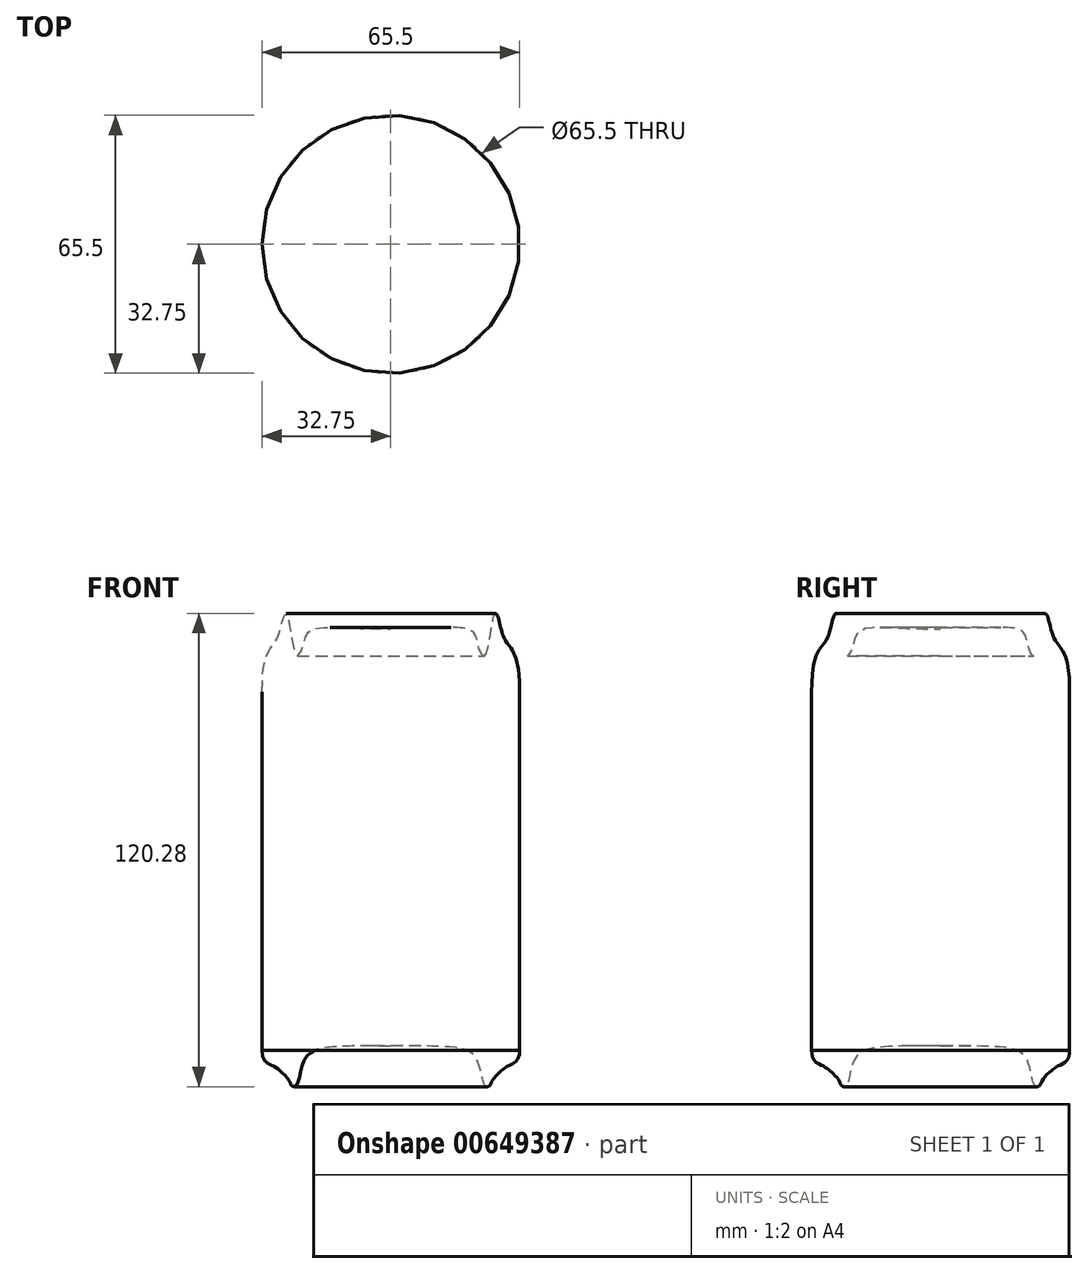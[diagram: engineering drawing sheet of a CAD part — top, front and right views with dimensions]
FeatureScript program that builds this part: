
annotation { "Feature Type Name" : "Feature", "Feature Type Description" : "" }
export const myFeature = defineFeature(function(context is Context, id is Id, definition is map)
    precondition{}
    {
        {
            var Q0;
            Q0=qCreatedBy(makeId("Front.planeOp"),FACE);
            var sketch = newSketch(context, id + "F0", { "sketchPlane" : qUnion([Q0])});
            skFitSpline(sketch, "E0", {"points": [v(0, 10) * mm, v(-15, 9.84) * mm, v(-21.6, 7.18) * mm, v(-24.03, 0) * mm, v(-25.14, 0) * mm, v(-25.75, 1.2) * mm, v(-29.73, 4.98) * mm, v(-32.75, 9) * mm], "startDerivative": vector(-99.34, 2.16) * mm, "endDerivative": vector(-0.76, 66.18) * mm});
            skLineSegment(sketch, "E1", {"start": v(-32.75, 9) * mm, "end": v(-32.75, 100) * mm});
            skFitSpline(sketch, "E2", {"points": [v(-32.75, 100) * mm, v(-29.56, 112.52) * mm, v(-28.34, 114.92) * mm, v(-27.59, 117.87) * mm, v(-26.5, 120) * mm, v(-23.97, 109.32) * mm, v(-22.5, 110.96) * mm, v(-21.2, 114.97) * mm, v(0, 116) * mm], "startDerivative": vector(-1.45, 158.98) * mm, "endDerivative": vector(201.28, -4.36) * mm});
            skLineSegment(sketch, "E3", {"start": v(0, 0) * mm, "end": v(0, 7.64) * mm});
            skSolve(sketch);
        }
        {
            var Q0;
            Q0=sQuery(id+"F0.wireOp",EDGE,"E0");
            var Q1;
            Q1=sQuery(id+"F0.wireOp",EDGE,"E1");
            var Q2;
            Q2=sQuery(id+"F0.wireOp",EDGE,"E2");
            var Q3;
            Q3=sQuery(id+"F0.wireOp",EDGE,"E3");
            revolve(context, id + "F1", {"bodyType" : ToolBodyType.SURFACE, "surfaceEntities" : qUnion([Q0, Q1, Q2]), "axis" : qUnion([Q3]), "revolveType" : RevolveType.FULL});
        }
    });
